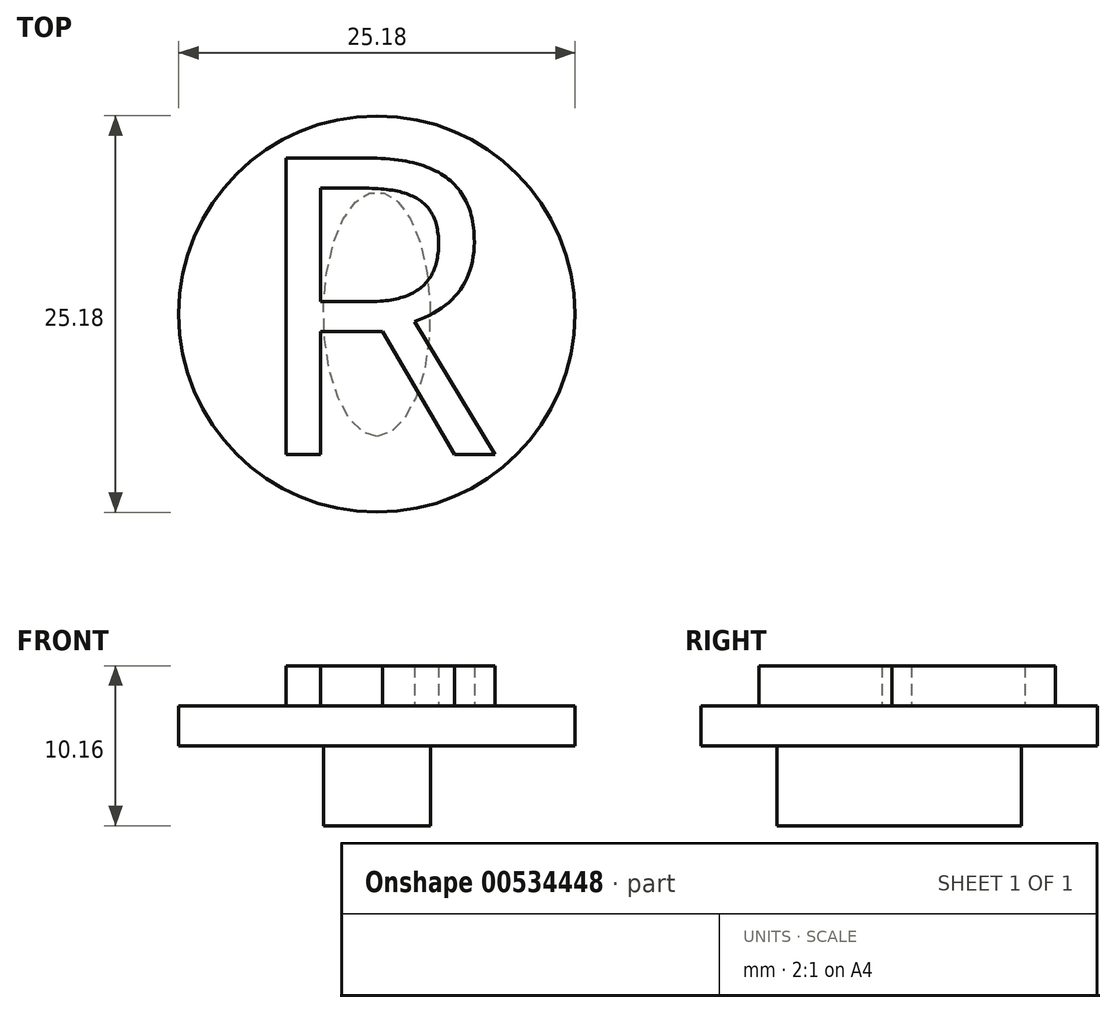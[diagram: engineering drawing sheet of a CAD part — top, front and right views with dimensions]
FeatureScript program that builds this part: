
annotation { "Feature Type Name" : "Feature", "Feature Type Description" : "" }
export const myFeature = defineFeature(function(context is Context, id is Id, definition is map)
    precondition{}
    {
        {
            var Q0;
            Q0=qCreatedBy(makeId("Top.planeOp"),FACE);
            var sketch = newSketch(context, id + "F0", { "sketchPlane" : qUnion([Q0])});
            skText(sketch, "E0", { "text": "R", "fontName": "OpenSans-Regular.ttf"});
            const initialGuessF0  = {"E0": [-0.03166, -0.0049, 1, 0, 0.019]};
            skSetInitialGuess(sketch, initialGuessF0);
            skSolve(sketch);
        }
        {
            var Q0;
            Q0 = qSketchRegion(id + "F0", true);
            extrude(context, id + "F1", {"entities" : qUnion([Q0]), "depth" : 5.08 * mm, "offsetDistance" : 25.4 * mm});
        }
        {
            var Q0;
            Q0=qCreatedBy(makeId("Top.planeOp"),FACE);
            var sketch = newSketch(context, id + "F2", { "sketchPlane" : qUnion([Q0])});
            skCircle(sketch, "E1", {"center": v(-23.31, 4.03) * mm, "radius": 12.59 * mm});
            skSolve(sketch);
        }
        {
            var Q0;
            Q0 = qSketchRegion(id + "F2", true);
            extrude(context, id + "F3", {"entities" : qUnion([Q0]), "operationType" : NewBodyOperationType.ADD, "depth" : 2.54 * mm, "offsetDistance" : 25.4 * mm});
        }
        {
            var Q0;
            Q0=makeQuery(id+"F3.boolean.opBoolean","MERGE",FACE,{"derivedFrom":[makeQuery(id+"F1.opExtrude","CAP_FACE",FACE,{"disambiguationData":[OSD([sQuery(id+"F0.wireOp",EDGE,"E0.sketch_text.stroke-0"),sQuery(id+"F0.wireOp",EDGE,"E0.sketch_text.stroke-1"),sQuery(id+"F0.wireOp",EDGE,"E0.sketch_text.stroke-2"),sQuery(id+"F0.wireOp",EDGE,"E0.sketch_text.stroke-3"),sQuery(id+"F0.wireOp",EDGE,"E0.sketch_text.stroke-4"),sQuery(id+"F0.wireOp",EDGE,"E0.sketch_text.stroke-5"),sQuery(id+"F0.wireOp",EDGE,"E0.sketch_text.stroke-6"),sQuery(id+"F0.wireOp",EDGE,"E0.sketch_text.stroke-7"),sQuery(id+"F0.wireOp",EDGE,"E0.sketch_text.stroke-8"),sQuery(id+"F0.wireOp",EDGE,"E0.sketch_text.stroke-9"),sQuery(id+"F0.wireOp",EDGE,"E0.sketch_text.stroke-10"),sQuery(id+"F0.wireOp",EDGE,"E0.sketch_text.stroke-11"),sQuery(id+"F0.wireOp",EDGE,"E0.sketch_text.stroke-12"),sQuery(id+"F0.wireOp",EDGE,"E0.sketch_text.stroke-13"),sQuery(id+"F0.wireOp",EDGE,"E0.sketch_text.stroke-14"),sQuery(id+"F0.wireOp",EDGE,"E0.sketch_text.stroke-15"),sQuery(id+"F0.wireOp",EDGE,"E0.sketch_text.stroke-16"),sQuery(id+"F0.wireOp",EDGE,"E0.sketch_text.stroke-17")])],"isStart":true}),makeQuery(id+"F3.opExtrude","CAP_FACE",FACE,{"disambiguationData":[OSD([sQuery(id+"F2.wireOp",EDGE,"E1")])],"isStart":true})]});
            var sketch = newSketch(context, id + "F4", { "sketchPlane" : qUnion([Q0])});
            skEllipse(sketch, "E2", {"center": v(-23.31, -4.03) * mm, "majorRadius": 7.77 * mm, "minorRadius": 3.4 * mm, "majorAxis": v(0, 1)});
            skSolve(sketch);
        }
        {
            var Q0;
            Q0 = qSketchRegion(id + "F4", true);
            extrude(context, id + "F5", {"entities" : qUnion([Q0]), "operationType" : NewBodyOperationType.ADD, "depth" : 5.08 * mm, "offsetDistance" : 25.4 * mm});
        }
    });
